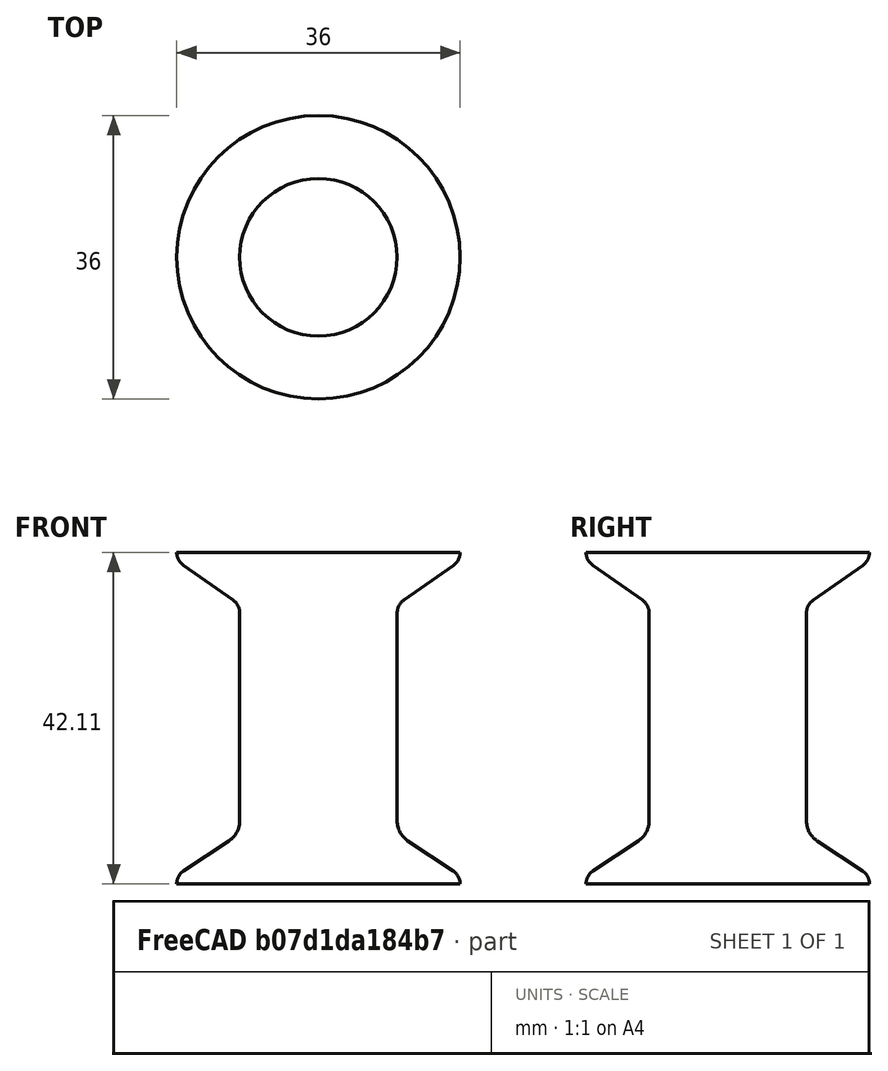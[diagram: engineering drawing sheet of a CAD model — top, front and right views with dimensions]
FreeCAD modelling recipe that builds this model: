
FCSTD DOCUMENT  (FreeCAD 0.20R29177 (Git))
Label: IntestineV3_outer
License: All rights reserved
LicenseURL: http://en.wikipedia.org/wiki/All_rights_reserved
objects: Sketcher::SketchObject×1, Part::Revolution×1, Part::Reverse×1
note: 3 computed .brp shape members not serialized (recipe doc carries the construction recipe); baked Part::Feature solids carry a one-line shape summary decoded from their .brp

FEATURE [Sketcher::SketchObject] Sketch
  FullyConstrained = false
  Placement = pos=(0,0,0) rot=(1,0,0;1.5708rad)
  sketch-geometry (13):
    g0: LineSegment StartX=10 StartY=73.3558 StartZ=0 EndX=10 EndY=46.9213 EndZ=0
    g1: LineSegment StartX=10.8526 StartY=74.994 StartZ=0 EndX=17.1474 EndY=79.4028 EndZ=0
    g2: LineSegment StartX=11.3405 StartY=44.4221 StartZ=0 EndX=17.1064 EndY=40.5934 EndZ=0
    g3: ArcOfCircle CenterX=16 CenterY=81.041 CenterZ=0 NormalX=0 NormalY=0 NormalZ=1 AngleXU=0 Radius=2 StartAngle=5.32338 EndAngle=6.28319
    g4: GeomPoint X=18 Y=80 Z=0
    g5: GeomPoint X=16.5 Y=80 Z=0
    g6: ArcOfCircle CenterX=12 CenterY=73.3558 CenterZ=0 NormalX=0 NormalY=0 NormalZ=1 AngleXU=0 Radius=2 StartAngle=2.18179 EndAngle=3.14159
    g7: GeomPoint X=10 Y=74.3968 Z=0
    g8: ArcOfCircle CenterX=13 CenterY=46.9213 CenterZ=0 NormalX=0 NormalY=0 NormalZ=1 AngleXU=0 Radius=3 StartAngle=3.14159 EndAngle=4.12621
    g9: GeomPoint X=10 Y=45.3123 Z=0
    g10: GeomPoint X=16.5 Y=40 Z=0
    g11: ArcOfCircle CenterX=16 CenterY=38.9273 CenterZ=0 NormalX=0 NormalY=0 NormalZ=1 AngleXU=0 Radius=2 StartAngle=1.4e-15 EndAngle=0.98462
    g12: GeomPoint X=18 Y=40 Z=0
  constraints (21):
    c: Vertical(g0)
    c: DistanceX(g-1,g7) = 10
    c: PointOnObject(g4,g1)
    c: Tangent(g1,g3) = -1.5708
    c: PointOnObject(g7,g1)
    c: PointOnObject(g7,g0)
    c: Tangent(g1,g6) = 1.5708
    c: Tangent(g0,g6) = -1.5708
    c: PointOnObject(g9,g0)
    c: PointOnObject(g9,g2)
    c: Tangent(g0,g8) = -1.5708
    c: Tangent(g2,g8) = -1.5708
    c: PointOnObject(g12,g2)
    c: Tangent(g2,g11) = 1.5708
    c: DistanceY(g4,g5) = 0
    c: DistanceY(g-1,g12) = 40
    c: Radius(g3) = 2
    c: Radius(g6) = 2
    c: Radius(g8) = 3
    c: Radius(g11) = 2
    c: DistanceY(g12,g10) = 0
FEATURE [Part::Revolution] Revolve
  Angle = 360
  Axis = (0,0,1)
  Base = (0,0,0)
  FaceMakerClass = Part::FaceMakerBullseye
  Solid = false
  Source = -> Sketch
  Symmetric = false
FEATURE [Part::Reverse] Revolve_rev  label="Revolve (Rev)"
  Source = -> Revolve
